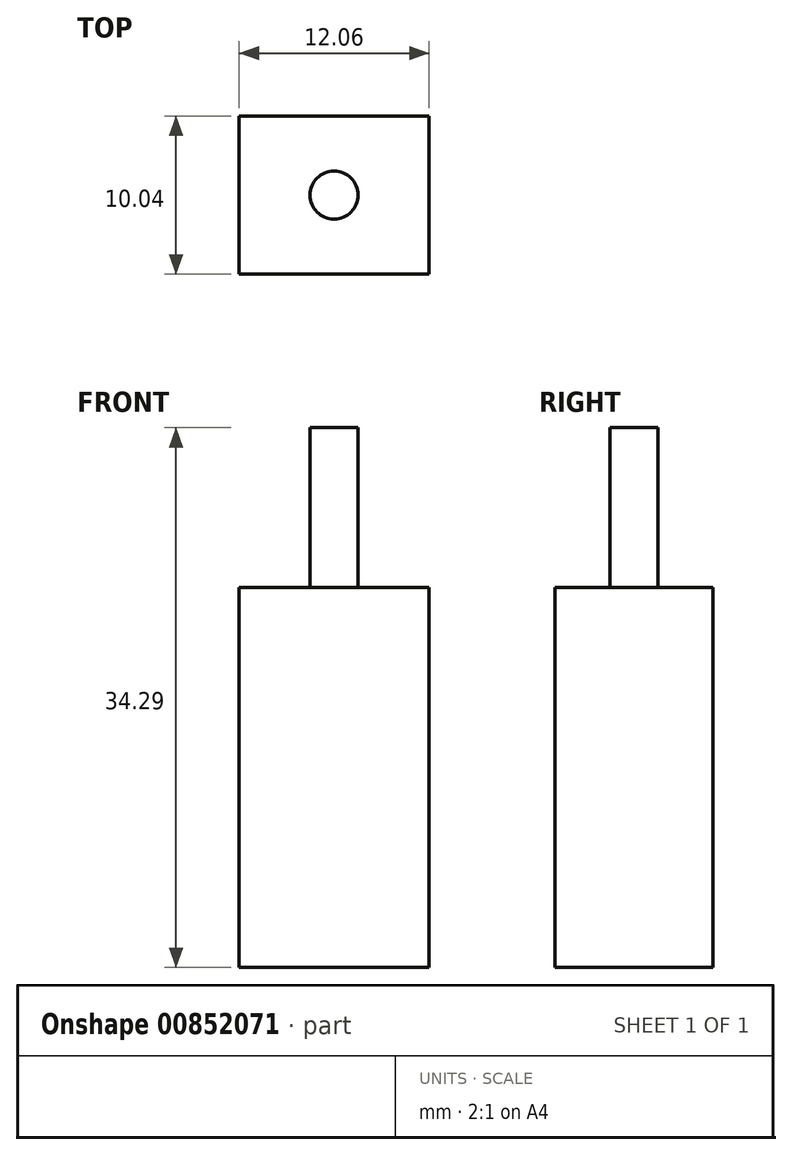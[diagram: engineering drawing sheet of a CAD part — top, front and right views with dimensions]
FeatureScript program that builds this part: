
annotation { "Feature Type Name" : "Feature", "Feature Type Description" : "" }
export const myFeature = defineFeature(function(context is Context, id is Id, definition is map)
    precondition{}
    {
        {
            var Q0;
            Q0=qCreatedBy(makeId("Top.planeOp"),FACE);
            var sketch = newSketch(context, id + "F0", { "sketchPlane" : qUnion([Q0])});
            skLineSegment(sketch, "E0.bottom", {"start": v(-6.03, 5.02) * mm, "end": v(6.03, 5.02) * mm});
            skLineSegment(sketch, "E0.top", {"start": v(-6.03, -5.02) * mm, "end": v(6.03, -5.02) * mm});
            skLineSegment(sketch, "E0.left", {"start": v(-6.03, 5.02) * mm, "end": v(-6.03, -5.02) * mm});
            skLineSegment(sketch, "E0.right", {"start": v(6.03, 5.02) * mm, "end": v(6.03, -5.02) * mm});
            skLineSegment(sketch, "E1", {"start": v(-6.03, 5.02) * mm, "end": v(6.03, -5.02) * mm, "construction": true});
            skSolve(sketch);
        }
        {
            var Q0;
            Q0 = qSketchRegion(id + "F0", true);
            extrude(context, id + "F1", {"entities" : qUnion([Q0]), "depth" : 24.13 * mm, "offsetDistance" : 25.4 * mm});
        }
        {
            var Q0;
            Q0=makeQuery(id+"F1.opExtrude","CAP_FACE",FACE,{"disambiguationData":[OSD([sQuery(id+"F0.wireOp",EDGE,"E0.bottom"),sQuery(id+"F0.wireOp",EDGE,"E0.top"),sQuery(id+"F0.wireOp",EDGE,"E0.left"),sQuery(id+"F0.wireOp",EDGE,"E0.right")])],"isStart":false});
            var sketch = newSketch(context, id + "F2", { "sketchPlane" : qUnion([Q0])});
            skCircle(sketch, "E2", {"center": v(0, 0) * mm, "radius": 1.52 * mm});
            skSolve(sketch);
        }
        {
            var Q0;
            Q0 = qSketchRegion(id + "F2", true);
            extrude(context, id + "F3", {"entities" : qUnion([Q0]), "operationType" : NewBodyOperationType.ADD, "depth" : 10.16 * mm, "offsetDistance" : 25.4 * mm});
        }
    });
